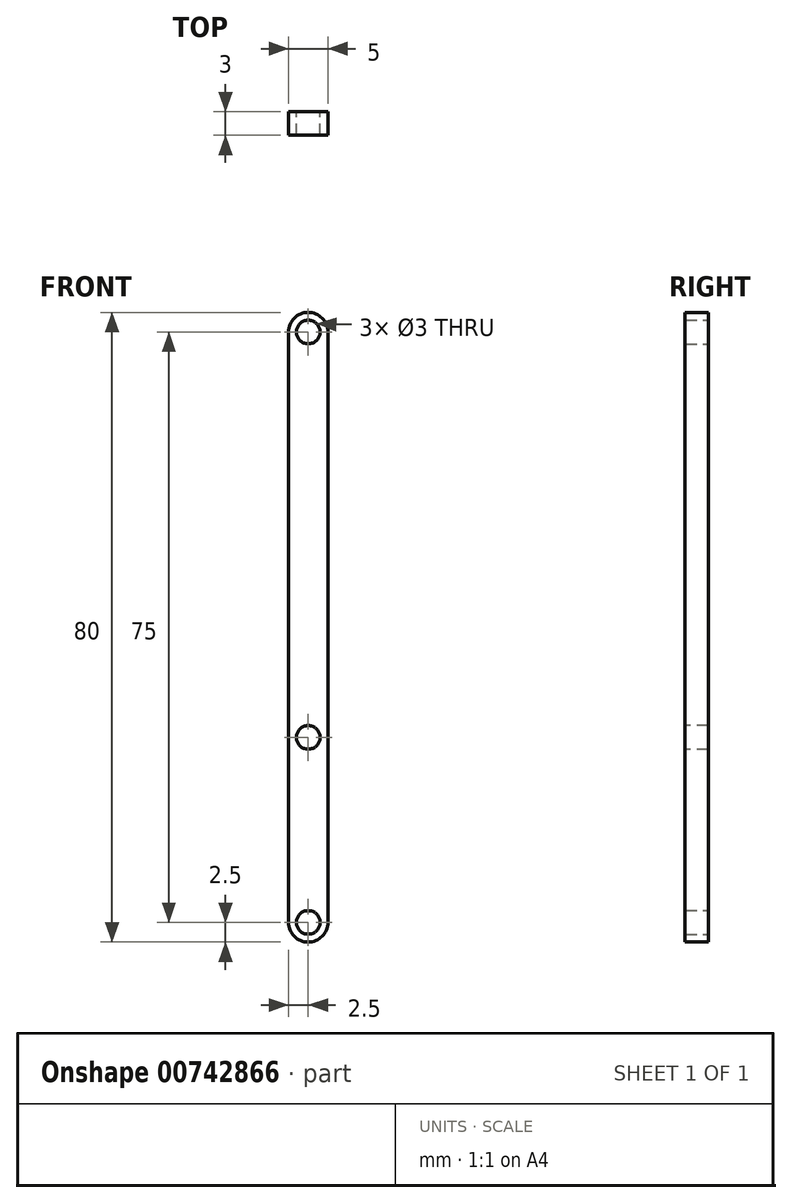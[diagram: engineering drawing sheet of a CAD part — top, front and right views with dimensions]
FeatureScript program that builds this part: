
annotation { "Feature Type Name" : "Feature", "Feature Type Description" : "" }
export const myFeature = defineFeature(function(context is Context, id is Id, definition is map)
    precondition{}
    {
        {
            var Q0;
            Q0=qCreatedBy(makeId("Front.planeOp"),FACE);
            var sketch = newSketch(context, id + "F0", { "sketchPlane" : qUnion([Q0])});
            skLineSegment(sketch, "E0.bottom", {"start": v(2.5, 37.5) * mm, "end": v(-2.5, 37.5) * mm, "construction": true});
            skLineSegment(sketch, "E0.top", {"start": v(2.5, -37.5) * mm, "end": v(-2.5, -37.5) * mm, "construction": true});
            skLineSegment(sketch, "E0.left", {"start": v(2.5, 37.5) * mm, "end": v(2.5, -37.5) * mm});
            skLineSegment(sketch, "E0.right", {"start": v(-2.5, 37.5) * mm, "end": v(-2.5, -37.5) * mm});
            skPoint(sketch, "E0.middle", {"position": v(0, 0) * mm});
            skArc(sketch, "E1", {"start": v(2.5, 37.5) * mm, "mid": v(0, 40) * mm, "end": v(-2.5, 37.5) * mm});
            skArc(sketch, "E2", {"start": v(-2.5, -37.5) * mm, "mid": v(0, -40) * mm, "end": v(2.5, -37.5) * mm});
            skCircle(sketch, "E3", {"center": v(0, 37.5) * mm, "radius": 1.5 * mm});
            skCircle(sketch, "E4", {"center": v(0, -37.5) * mm, "radius": 1.5 * mm});
            skSolve(sketch);
        }
        {
            var Q0;
            Q0 = qSketchRegion(id + "F0", true);
            extrude(context, id + "F1", {"entities" : qUnion([Q0]), "depth" : 3 * mm, "offsetDistance" : 25 * mm});
        }
        {
            var Q0;
            Q0=makeQuery(id+"F1.opExtrude","CAP_FACE",FACE,{"disambiguationData":[OSD([sQuery(id+"F0.wireOp",EDGE,"E0.left"),sQuery(id+"F0.wireOp",EDGE,"E0.right"),sQuery(id+"F0.wireOp",EDGE,"E1"),sQuery(id+"F0.wireOp",EDGE,"E2"),sQuery(id+"F0.wireOp",EDGE,"E3"),sQuery(id+"F0.wireOp",EDGE,"E4")])],"isStart":false});
            var sketch = newSketch(context, id + "F2", { "sketchPlane" : qUnion([Q0])});
            skCircle(sketch, "E5", {"center": v(0, -14) * mm, "radius": 1.5 * mm});
            skSolve(sketch);
        }
        {
            var Q0;
            Q0=makeQuery(id+"F2.imprint","IMPRINT",FACE,{"disambiguationData":[TD([[makeQuery(id+"F2.imprint","IMPRINT",EDGE,{"derivedFrom":sQuery(id+"F2.wireOp",EDGE,"E5")}),1.0]])]});
            extrude(context, id + "F3", {"entities" : qUnion([Q0]), "operationType" : NewBodyOperationType.REMOVE, "oppositeDirection" : true, "depth" : 25 * mm, "offsetDistance" : 25 * mm});
        }
    });
